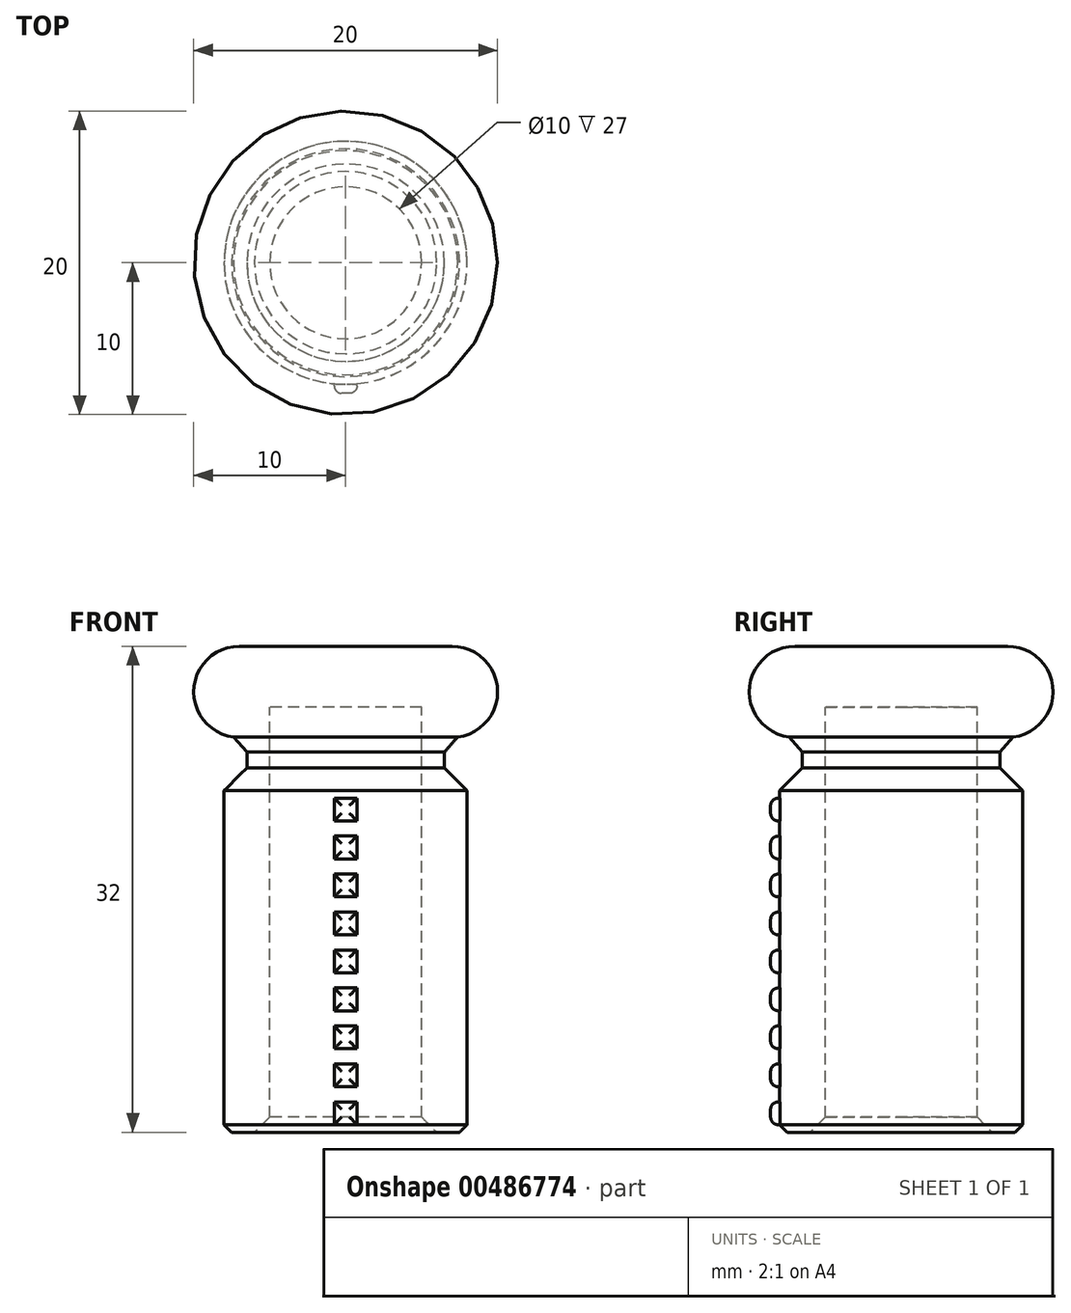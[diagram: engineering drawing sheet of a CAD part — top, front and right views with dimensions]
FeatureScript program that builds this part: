
annotation { "Feature Type Name" : "Feature", "Feature Type Description" : "" }
export const myFeature = defineFeature(function(context is Context, id is Id, definition is map)
    precondition{}
    {
        {
            var Q0;
            Q0=qCreatedBy(makeId("Front.planeOp"),FACE);
            var sketch = newSketch(context, id + "F0", { "sketchPlane" : qUnion([Q0])});
            skLineSegment(sketch, "E0", {"start": v(-5, 0) * mm, "end": v(-8, 0) * mm});
            skLineSegment(sketch, "E1", {"start": v(-5, 0) * mm, "end": v(-5, 28) * mm});
            skLineSegment(sketch, "E2", {"start": v(-5, 28) * mm, "end": v(0, 28) * mm});
            skLineSegment(sketch, "E3", {"start": v(-8, 0) * mm, "end": v(-8, 23) * mm});
            skArc(sketch, "E4", {"start": v(-7, 32) * mm, "mid": v(-10, 29) * mm, "end": v(-7, 26) * mm});
            skLineSegment(sketch, "E5", {"start": v(-7, 32) * mm, "end": v(0, 32) * mm});
            skLineSegment(sketch, "E6", {"start": v(0, 32) * mm, "end": v(0, 28) * mm});
            skLineSegment(sketch, "E7", {"start": v(-7, 26) * mm, "end": v(-6.5, 26) * mm});
            skLineSegment(sketch, "E8", {"start": v(-8, 23) * mm, "end": v(-6.5, 23) * mm});
            skLineSegment(sketch, "E9", {"start": v(-6.5, 23) * mm, "end": v(-6.5, 26) * mm});
            skSolve(sketch);
        }
        {
            var Q0;
            Q0=makeQuery(id+"F0.imprint","IMPRINT",FACE,{"disambiguationData":[TD([[makeQuery(id+"F0.imprint","IMPRINT",EDGE,{"derivedFrom":sQuery(id+"F0.wireOp",EDGE,"E0")}),-1.0]])]});
            var Q1;
            Q1=sQuery(id+"F0.wireOp",EDGE,"E6");
            revolve(context, id + "F1", {"entities" : qUnion([Q0]), "axis" : qUnion([Q1]), "revolveType" : RevolveType.FULL});
        }
        {
            var Q0;
            Q0=qCreatedBy(makeId("Front.planeOp"),FACE);
            cPlane(context, id + "F2", {"entities" : qUnion([Q0]), "cplaneType" : CPlaneType.OFFSET, "offset" : 7 * mm, "width" : 150 * mm, "height" : 150 * mm});
        }
        {
            var Q0;
            Q0=qCreatedBy(id+"F2.planeOp",FACE);
            var sketch = newSketch(context, id + "F3", { "sketchPlane" : qUnion([Q0])});
            skLineSegment(sketch, "E10.bottom", {"start": v(0.75, 20.5) * mm, "end": v(-0.75, 20.5) * mm});
            skLineSegment(sketch, "E10.top", {"start": v(0.75, 22) * mm, "end": v(-0.75, 22) * mm});
            skLineSegment(sketch, "E10.left", {"start": v(0.75, 20.5) * mm, "end": v(0.75, 22) * mm});
            skLineSegment(sketch, "E10.right", {"start": v(-0.75, 20.5) * mm, "end": v(-0.75, 22) * mm});
            skPoint(sketch, "E10.middle", {"position": v(0, 21.25) * mm});
            skLineSegment(sketch, "E11.1.0.0", {"start": v(-0.75, 18) * mm, "end": v(-0.75, 19.5) * mm});
            skLineSegment(sketch, "E11.1.0.1", {"start": v(0.75, 18) * mm, "end": v(-0.75, 18) * mm});
            skLineSegment(sketch, "E11.1.0.2", {"start": v(0.75, 18) * mm, "end": v(0.75, 19.5) * mm});
            skLineSegment(sketch, "E11.1.0.3", {"start": v(0.75, 19.5) * mm, "end": v(-0.75, 19.5) * mm});
            skLineSegment(sketch, "E11.2.0.0", {"start": v(-0.75, 15.5) * mm, "end": v(-0.75, 17) * mm});
            skLineSegment(sketch, "E11.2.0.1", {"start": v(0.75, 15.5) * mm, "end": v(-0.75, 15.5) * mm});
            skLineSegment(sketch, "E11.2.0.2", {"start": v(0.75, 15.5) * mm, "end": v(0.75, 17) * mm});
            skLineSegment(sketch, "E11.2.0.3", {"start": v(0.75, 17) * mm, "end": v(-0.75, 17) * mm});
            skLineSegment(sketch, "E11.direction1", {"start": v(-0.75, 20.5) * mm, "end": v(-0.75, 18) * mm, "construction": true});
            skLineSegment(sketch, "E12.0.3.0", {"start": v(-0.75, 13) * mm, "end": v(-0.75, 14.5) * mm});
            skLineSegment(sketch, "E12.3.3.0", {"start": v(0.75, 13) * mm, "end": v(-0.75, 13) * mm});
            skLineSegment(sketch, "E12.6.3.0", {"start": v(0.75, 13) * mm, "end": v(0.75, 14.5) * mm});
            skLineSegment(sketch, "E12.9.3.0", {"start": v(0.75, 14.5) * mm, "end": v(-0.75, 14.5) * mm});
            skLineSegment(sketch, "E12.0.4.0", {"start": v(-0.75, 10.5) * mm, "end": v(-0.75, 12) * mm});
            skLineSegment(sketch, "E12.3.4.0", {"start": v(0.75, 10.5) * mm, "end": v(-0.75, 10.5) * mm});
            skLineSegment(sketch, "E12.6.4.0", {"start": v(0.75, 10.5) * mm, "end": v(0.75, 12) * mm});
            skLineSegment(sketch, "E12.9.4.0", {"start": v(0.75, 12) * mm, "end": v(-0.75, 12) * mm});
            skLineSegment(sketch, "E12.0.5.0", {"start": v(-0.75, 8) * mm, "end": v(-0.75, 9.5) * mm});
            skLineSegment(sketch, "E12.3.5.0", {"start": v(0.75, 8) * mm, "end": v(-0.75, 8) * mm});
            skLineSegment(sketch, "E12.6.5.0", {"start": v(0.75, 8) * mm, "end": v(0.75, 9.5) * mm});
            skLineSegment(sketch, "E12.9.5.0", {"start": v(0.75, 9.5) * mm, "end": v(-0.75, 9.5) * mm});
            skLineSegment(sketch, "E12.0.6.0", {"start": v(-0.75, 5.5) * mm, "end": v(-0.75, 7) * mm});
            skLineSegment(sketch, "E12.3.6.0", {"start": v(0.75, 5.5) * mm, "end": v(-0.75, 5.5) * mm});
            skLineSegment(sketch, "E12.6.6.0", {"start": v(0.75, 5.5) * mm, "end": v(0.75, 7) * mm});
            skLineSegment(sketch, "E12.9.6.0", {"start": v(0.75, 7) * mm, "end": v(-0.75, 7) * mm});
            skLineSegment(sketch, "E12.0.7.0", {"start": v(-0.75, 3) * mm, "end": v(-0.75, 4.5) * mm});
            skLineSegment(sketch, "E12.3.7.0", {"start": v(0.75, 3) * mm, "end": v(-0.75, 3) * mm});
            skLineSegment(sketch, "E12.6.7.0", {"start": v(0.75, 3) * mm, "end": v(0.75, 4.5) * mm});
            skLineSegment(sketch, "E12.9.7.0", {"start": v(0.75, 4.5) * mm, "end": v(-0.75, 4.5) * mm});
            skLineSegment(sketch, "E13.0.8.0", {"start": v(-0.75, 0.5) * mm, "end": v(-0.75, 2) * mm});
            skLineSegment(sketch, "E13.3.8.0", {"start": v(0.75, 0.5) * mm, "end": v(-0.75, 0.5) * mm});
            skLineSegment(sketch, "E13.6.8.0", {"start": v(0.75, 0.5) * mm, "end": v(0.75, 2) * mm});
            skLineSegment(sketch, "E13.9.8.0", {"start": v(0.75, 2) * mm, "end": v(-0.75, 2) * mm});
            skSolve(sketch);
        }
        {
            var Q0;
            Q0 = qSketchRegion(id + "F3", true);
            extrude(context, id + "F4", {"entities" : qUnion([Q0]), "operationType" : NewBodyOperationType.ADD, "depth" : 1.6 * mm});
        }
        {
            var Q0;
            Q0=makeQuery(id+"F4.opExtrude","CAP_FACE",FACE,{"disambiguationData":[OSD([sQuery(id+"F3.wireOp",EDGE,"E10.bottom"),sQuery(id+"F3.wireOp",EDGE,"E10.top"),sQuery(id+"F3.wireOp",EDGE,"E10.left"),sQuery(id+"F3.wireOp",EDGE,"E10.right")])],"isStart":false});
            var Q1;
            Q1=makeQuery(id+"F4.opExtrude","CAP_FACE",FACE,{"disambiguationData":[OSD([sQuery(id+"F3.wireOp",EDGE,"E11.1.0.0"),sQuery(id+"F3.wireOp",EDGE,"E11.1.0.1"),sQuery(id+"F3.wireOp",EDGE,"E11.1.0.2"),sQuery(id+"F3.wireOp",EDGE,"E11.1.0.3")])],"isStart":false});
            var Q2;
            Q2=makeQuery(id+"F4.opExtrude","CAP_FACE",FACE,{"disambiguationData":[OSD([sQuery(id+"F3.wireOp",EDGE,"E11.2.0.0"),sQuery(id+"F3.wireOp",EDGE,"E11.2.0.1"),sQuery(id+"F3.wireOp",EDGE,"E11.2.0.2"),sQuery(id+"F3.wireOp",EDGE,"E11.2.0.3")])],"isStart":false});
            var Q3;
            Q3=makeQuery(id+"F4.opExtrude","CAP_FACE",FACE,{"disambiguationData":[OSD([sQuery(id+"F3.wireOp",EDGE,"E12.0.3.0"),sQuery(id+"F3.wireOp",EDGE,"E12.3.3.0"),sQuery(id+"F3.wireOp",EDGE,"E12.6.3.0"),sQuery(id+"F3.wireOp",EDGE,"E12.9.3.0")])],"isStart":false});
            var Q4;
            Q4=makeQuery(id+"F4.opExtrude","CAP_FACE",FACE,{"disambiguationData":[OSD([sQuery(id+"F3.wireOp",EDGE,"E12.0.4.0"),sQuery(id+"F3.wireOp",EDGE,"E12.3.4.0"),sQuery(id+"F3.wireOp",EDGE,"E12.6.4.0"),sQuery(id+"F3.wireOp",EDGE,"E12.9.4.0")])],"isStart":false});
            var Q5;
            Q5=makeQuery(id+"F4.opExtrude","CAP_FACE",FACE,{"disambiguationData":[OSD([sQuery(id+"F3.wireOp",EDGE,"E12.0.5.0"),sQuery(id+"F3.wireOp",EDGE,"E12.3.5.0"),sQuery(id+"F3.wireOp",EDGE,"E12.6.5.0"),sQuery(id+"F3.wireOp",EDGE,"E12.9.5.0")])],"isStart":false});
            var Q6;
            Q6=makeQuery(id+"F4.opExtrude","CAP_FACE",FACE,{"disambiguationData":[OSD([sQuery(id+"F3.wireOp",EDGE,"E12.0.6.0"),sQuery(id+"F3.wireOp",EDGE,"E12.3.6.0"),sQuery(id+"F3.wireOp",EDGE,"E12.6.6.0"),sQuery(id+"F3.wireOp",EDGE,"E12.9.6.0")])],"isStart":false});
            var Q7;
            Q7=makeQuery(id+"F4.opExtrude","CAP_FACE",FACE,{"disambiguationData":[OSD([sQuery(id+"F3.wireOp",EDGE,"E12.0.7.0"),sQuery(id+"F3.wireOp",EDGE,"E12.3.7.0"),sQuery(id+"F3.wireOp",EDGE,"E12.6.7.0"),sQuery(id+"F3.wireOp",EDGE,"E12.9.7.0")])],"isStart":false});
            var Q8;
            Q8=makeQuery(id+"F4.opExtrude","CAP_FACE",FACE,{"disambiguationData":[OSD([sQuery(id+"F3.wireOp",EDGE,"E13.0.8.0"),sQuery(id+"F3.wireOp",EDGE,"E13.3.8.0"),sQuery(id+"F3.wireOp",EDGE,"E13.6.8.0"),sQuery(id+"F3.wireOp",EDGE,"E13.9.8.0")])],"isStart":false});
            fillet(context, id + "F5", {"entities" : qUnion([Q0, Q1, Q2, Q3, Q4, Q5, Q6, Q7, Q8]), "radius" : 0.5 * mm, "tangentPropagation" : true, "allowEdgeOverflow" : false});
        }
        {
            var Q0;
            Q0=makeQuery(id+"F1.opRevolve","SWEPT_EDGE",EDGE,{"disambiguationData":[OSD([sQuery(id+"F0.wireOp",EDGE,"E0"),sQuery(id+"F0.wireOp",EDGE,"E3")])]});
            var Q1;
            Q1=makeQuery(id+"F1.opRevolve","SWEPT_EDGE",EDGE,{"disambiguationData":[OSD([sQuery(id+"F0.wireOp",EDGE,"E3"),sQuery(id+"F0.wireOp",EDGE,"E8")])]});
            chamfer(context, id + "F6", {"entities" : qUnion([Q0, Q1]), "width" : 0.5 * mm, "tangentPropagation" : true});
        }
        {
            var Q0;
            Q0=makeQuery(id+"F1.opRevolve","SWEPT_EDGE",EDGE,{"disambiguationData":[OSD([sQuery(id+"F0.wireOp",EDGE,"E0"),sQuery(id+"F0.wireOp",EDGE,"E1")])]});
            chamfer(context, id + "F7", {"entities" : qUnion([Q0]), "width" : 1 * mm, "tangentPropagation" : true});
        }
        {
            var Q0;
            Q0=makeQuery(id+"F1.opRevolve","SWEPT_FACE",FACE,{"disambiguationData":[OSD([sQuery(id+"F0.wireOp",EDGE,"E9")])]});
            chamfer(context, id + "F8", {"entities" : qUnion([Q0]), "width" : 1 * mm, "tangentPropagation" : true});
        }
    });
